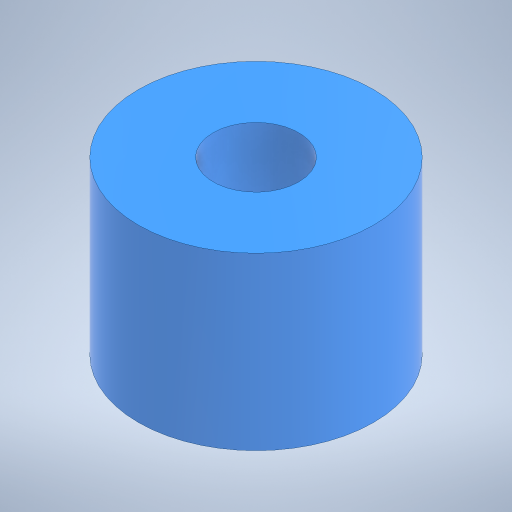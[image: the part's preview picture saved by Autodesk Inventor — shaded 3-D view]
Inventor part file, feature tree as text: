
AUTODESK INVENTOR PART (.ipt)
format: ipt  version: 2024 (Build 280153000, 153)  size: 212,480 bytes
history: native  units: in
note: dims shown in document units (in); Inventor stores cm internally (conversion verified against a paired STEP export)
features: extrude x1, sketch x1
ambient origin geometry x8: Origin, YZ Plane, XZ Plane, XY Plane, X Axis, Y Axis, Z Axis, Center Point
bodies: Solid1 (feature_tree)
feature tree (2):
  extrude  "Extrusion1"  Depth=0.5in
  sketch  "Sketch1"  dims[d0=0.6875in d1=0.25in d2=0.5in d3=0.0in]
